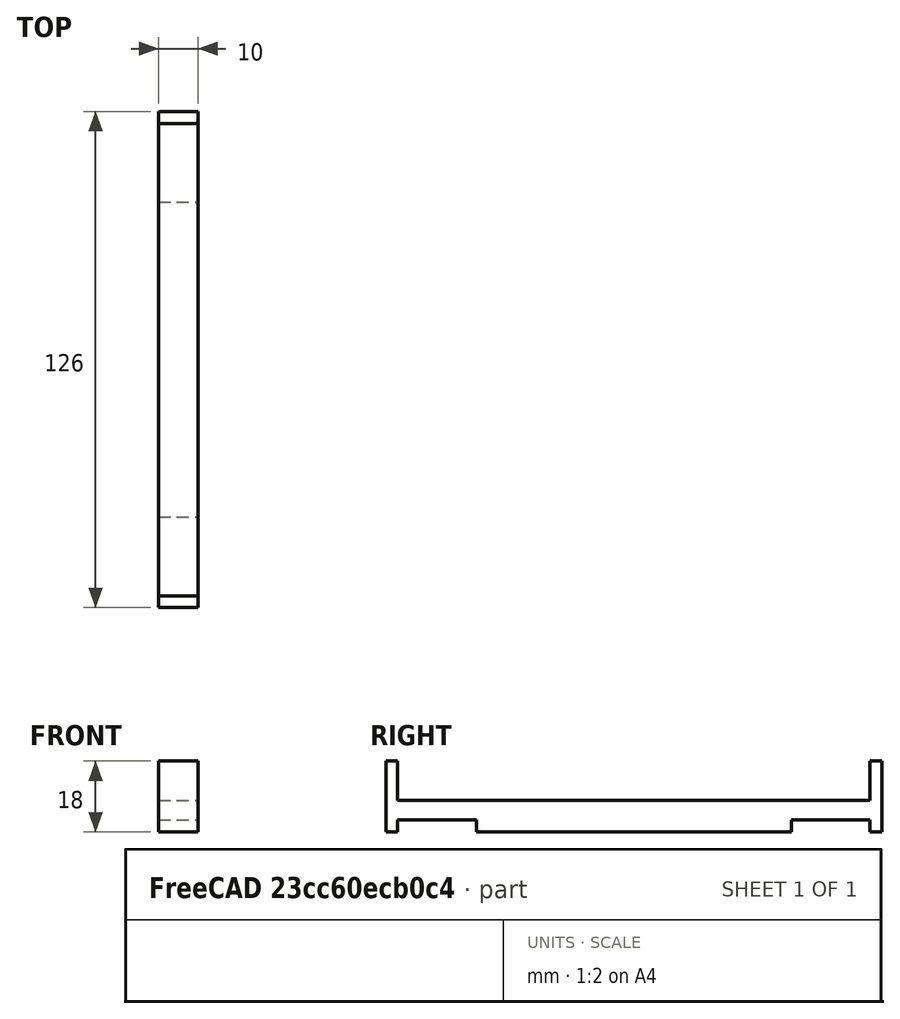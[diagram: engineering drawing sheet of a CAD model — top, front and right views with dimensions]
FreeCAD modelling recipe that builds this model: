
FCSTD DOCUMENT  (FreeCAD 0.20R25352 (Git))
Label: ebike battery holder
License: All rights reserved
LicenseURL: http://en.wikipedia.org/wiki/All_rights_reserved
objects: Sketcher::SketchObject×1, PartDesign::Pad×1, PartDesign::Body×1
note: 4 computed .brp shape members not serialized (recipe doc carries the construction recipe); baked Part::Feature solids carry a one-line shape summary decoded from their .brp

FEATURE [Sketcher::SketchObject] Sketch
  FullyConstrained = true
  MapMode = 5
  Placement = pos=(0,0,0) rot=(0.57735,0.57735,0.57735;2.0944rad)
  Support = -> [YZ_Plane]
  sketch-geometry (17):
    g0: LineSegment StartX=-63 StartY=0 StartZ=0 EndX=-63 EndY=18 EndZ=0
    g1: LineSegment StartX=-63 StartY=18 StartZ=0 EndX=-60 EndY=18 EndZ=0
    g2: LineSegment StartX=-60 StartY=18 StartZ=0 EndX=-60 EndY=8 EndZ=0
    g3: LineSegment StartX=-60 StartY=8 StartZ=0 EndX=60 EndY=8 EndZ=0
    g4: LineSegment StartX=60 StartY=8 StartZ=0 EndX=60 EndY=18 EndZ=0
    g5: LineSegment StartX=60 StartY=18 StartZ=0 EndX=63 EndY=18 EndZ=0
    g6: LineSegment StartX=63 StartY=18 StartZ=0 EndX=63 EndY=0 EndZ=0
    g7: LineSegment StartX=-63 StartY=0 StartZ=0 EndX=-60 EndY=0 EndZ=0
    g8: LineSegment StartX=-60 StartY=0 StartZ=0 EndX=-60 EndY=3 EndZ=0
    g9: LineSegment StartX=-60 StartY=3 StartZ=0 EndX=-40 EndY=3 EndZ=0
    g10: LineSegment StartX=-40 StartY=3 StartZ=0 EndX=-40 EndY=0 EndZ=0
    g11: LineSegment StartX=-40 StartY=0 StartZ=0 EndX=0 EndY=0 EndZ=0
    g12: LineSegment StartX=0 StartY=0 StartZ=0 EndX=40 EndY=0 EndZ=0
    g13: LineSegment StartX=40 StartY=0 StartZ=0 EndX=40 EndY=3 EndZ=0
    g14: LineSegment StartX=40 StartY=3 StartZ=0 EndX=60 EndY=3 EndZ=0
    g15: LineSegment StartX=60 StartY=3 StartZ=0 EndX=60 EndY=0 EndZ=0
    g16: LineSegment StartX=60 StartY=0 StartZ=0 EndX=63 EndY=0 EndZ=0
  constraints (44):
    c: PointOnObject(g0,g-1)
    c: Vertical(g0)
    c: Coincident(g0,g1)
    c: Horizontal(g1)
    c: Coincident(g1,g2)
    c: Vertical(g2)
    c: Coincident(g2,g3)
    c: Horizontal(g3)
    c: Coincident(g3,g4)
    c: Coincident(g4,g5)
    c: Coincident(g5,g6)
    c: PointOnObject(g6,g-1)
    c: Symmetric(g1,g4,g-2)
    c: Vertical(g4)
    c: Vertical(g6)
    c: Symmetric(g5,g0,g-2)
    c: DistanceX(g1,g1) = 3
    c: Coincident(g0,g7)
    c: PointOnObject(g7,g-1)
    c: Coincident(g7,g8)
    c: Vertical(g8)
    c: Coincident(g8,g9)
    c: Horizontal(g9)
    c: Coincident(g9,g10)
    c: PointOnObject(g10,g-1)
    c: Vertical(g10)
    c: Coincident(g10,g11)
    c: Coincident(g11,g-1)
    c: Coincident(g11,g12)
    c: Coincident(g12,g13)
    c: Coincident(g13,g14)
    c: Coincident(g14,g15)
    c: Coincident(g15,g16)
    c: Coincident(g16,g6)
    c: Symmetric(g15,g7,g-2)
    c: Symmetric(g10,g12,g11)
    c: Symmetric(g8,g14,g-2)
    c: Symmetric(g9,g13,g-2)
    c: DistanceY(g2,g2) = 10
    c: DistanceX(g3,g3) = 120
    c: DistanceX(g9,g13) = 80
    c: DistanceX(g9,g9) = 20
    c: DistanceY(g8,g8) = 3
    c: DistanceY(g8,g2) = 5
FEATURE [PartDesign::Pad] Pad
  Direction = (1,-2e-16,3e-16)
  Length = 10
  Length2 = 100
  Placement = pos=(0,0,0) rot=(0.57735,0.57735,0.57735;2.0944rad)
  Profile = -> Sketch
  Type = 0
FEATURE [PartDesign::Body] Body
  Group = -> [Sketch,Pad]
  Origin = -> Origin
  Tip = -> Pad
